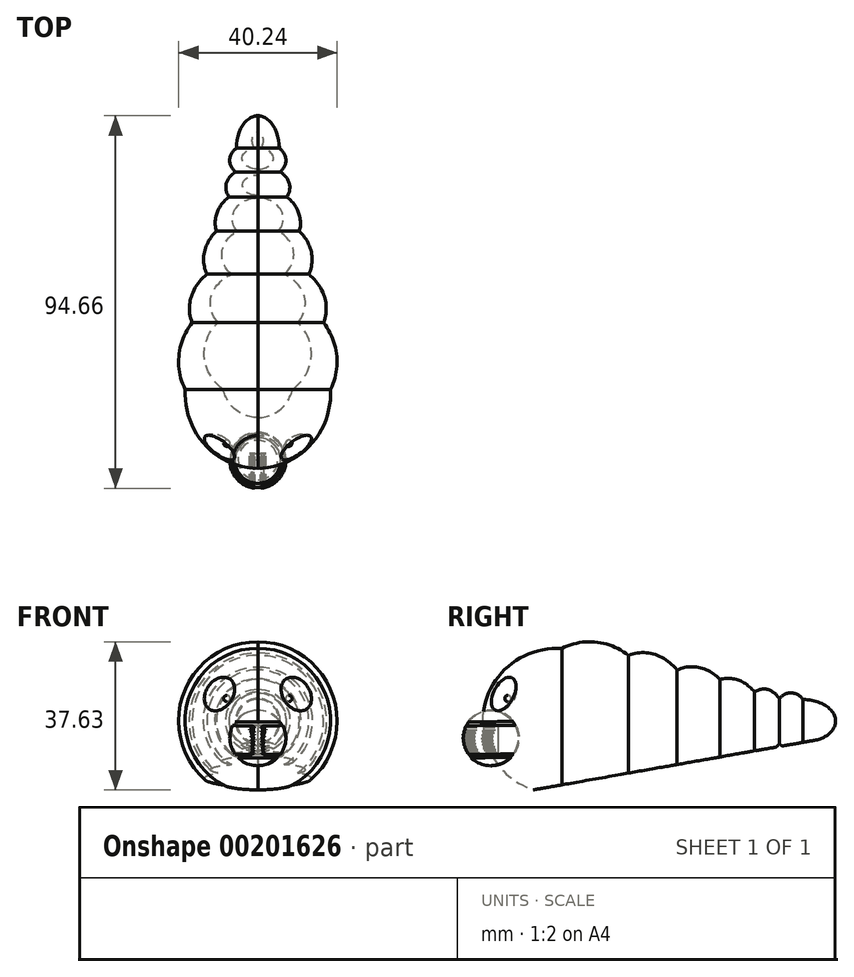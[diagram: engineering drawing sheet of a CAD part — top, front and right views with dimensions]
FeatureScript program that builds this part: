
annotation { "Feature Type Name" : "Feature", "Feature Type Description" : "" }
export const myFeature = defineFeature(function(context is Context, id is Id, definition is map)
    precondition{}
    {
        {
            var Q0;
            Q0=qCreatedBy(makeId("Top.planeOp"),FACE);
            var sketch = newSketch(context, id + "F0", { "sketchPlane" : qUnion([Q0])});
            skEllipticalArc(sketch, "E0", {});
            skEllipticalArc(sketch, "E1", {});
            skPoint(sketch, "E1.centerSnap0", {"position": v(0, -21.26) * mm});
            skEllipticalArc(sketch, "E2", {});
            skEllipticalArc(sketch, "E3", {});
            skEllipticalArc(sketch, "E4", {});
            skEllipticalArc(sketch, "E5", {});
            skEllipticalArc(sketch, "E6", {});
            skEllipticalArc(sketch, "E7", {});
            skLineSegment(sketch, "E8", {"start": v(0, 15.02) * mm, "end": v(0, -47.02) * mm});
            skLineSegment(sketch, "E9", {"start": v(0, -66.04) * mm, "end": v(0, 23.55) * mm});
            const initialGuessF0  = {"E0": [0, -0.038948312401771545, -1, 0, 0.0201253741979599, 0.017687600936562343, 2.7319737527427694, 3.735705464207903], "E1": [0, -0.025389280170202255, -1, 0, 0.017381285256523642, 0.012980058674735876, 2.8559072971359845, 3.8713688343084676], "E2": [0, -0.012964989989995956, -1, 0, 0.013778002209999156, 0.01107321615129807, 2.794142284714198, 3.8417705752233933], "E3": [0, -0.003726113587617874, -1, 0, 0.010834074892715644, 0.00903717395902369, 2.906642104325587, 3.9684165475596376], "E4": [0, 0.005311060371405817, -1, 0, 0.008132504217033262, 0.005535526062008481, 2.6956009997515697, 3.9359959156809072], "E5": [0, -0.04702418949455023, -1, 0, 0.01848768108972128, 0.019015910590964333, 1.5707963267948966, 3.195869498983652], "E6": [0, 0.012173164635896683, -1, 0, 0.007152805326904107, 0.0048193785957226605, 2.4925865913491534, 3.8422771913521236], "E7": [0, 0.015022817999124527, 0, -1, 0.008524764502291721, 0.005470109626082388, 1.6010185470610119, 3.141592653589793]};
            skSetInitialGuess(sketch, initialGuessF0);
            skSolve(sketch);
        }
        {
            var Q0;
            Q0=makeQuery(id+"F0.imprint","IMPRINT",FACE,{"disambiguationData":[TD([[makeQuery(id+"F0.imprint","IMPRINT",EDGE,{"derivedFrom":sQuery(id+"F0.wireOp",EDGE,"E0")}),1.0]])]});
            var Q1;
            Q1=sQuery(id+"F0.wireOp",EDGE,"E9");
            revolve(context, id + "F1", {"entities" : qUnion([Q0]), "axis" : qUnion([Q1]), "revolveType" : RevolveType.SYMMETRIC, "oppositeDirection" : true, "angle" : 180 * degree});
        }
        {
            var Q0;
            Q0=qCreatedBy(makeId("Top.planeOp"),FACE);
            cPlane(context, id + "F2", {"entities" : qUnion([Q0]), "cplaneType" : CPlaneType.OFFSET, "offset" : 8 * mm, "width" : 150 * mm, "height" : 150 * mm});
        }
        {
            var Q0;
            Q0=qCreatedBy(id+"F2.planeOp",FACE);
            var sketch = newSketch(context, id + "F3", { "sketchPlane" : qUnion([Q0])});
            skArc(sketch, "E10", {"start": v(11.4, -57.45) * mm, "mid": v(5.9, -62.94) * mm, "end": v(11.4, -68.44) * mm});
            skLineSegment(sketch, "E11", {"start": v(11.4, -68.44) * mm, "end": v(11.4, -62.94) * mm});
            skLineSegment(sketch, "E12", {"start": v(11.4, -62.94) * mm, "end": v(11.4, -57.45) * mm});
            skSolve(sketch);
        }
        {
            var Q0;
            Q0=makeQuery(id+"F3.imprint","IMPRINT",FACE,{"disambiguationData":[TD([[makeQuery(id+"F3.imprint","IMPRINT",EDGE,{"derivedFrom":sQuery(id+"F3.wireOp",EDGE,"E10")}),1.0]])]});
            var Q1;
            Q1=sQuery(id+"F3.wireOp",EDGE,"E11");
            revolve(context, id + "F4", {"entities" : qUnion([Q0]), "axis" : qUnion([Q1]), "revolveType" : RevolveType.FULL});
        }
        {
            var Q0;
            Q0=makeQuery(id+"F1.opRevolve","SWEPT_BODY",BODY,{"disambiguationData":[OSD([sQuery(id+"F0.wireOp",EDGE,"E0"),sQuery(id+"F0.wireOp",EDGE,"E1"),sQuery(id+"F0.wireOp",EDGE,"E2"),sQuery(id+"F0.wireOp",EDGE,"E3"),sQuery(id+"F0.wireOp",EDGE,"E4"),sQuery(id+"F0.wireOp",EDGE,"E5"),sQuery(id+"F0.wireOp",EDGE,"E6"),sQuery(id+"F0.wireOp",EDGE,"E7"),sQuery(id+"F0.wireOp",EDGE,"E9")])]});
            var Q1;
            Q1=makeQuery(id+"F1.opRevolve","CAP_FACE",FACE,{"disambiguationData":[OSD([sQuery(id+"F0.wireOp",EDGE,"E0"),sQuery(id+"F0.wireOp",EDGE,"E1"),sQuery(id+"F0.wireOp",EDGE,"E2"),sQuery(id+"F0.wireOp",EDGE,"E3"),sQuery(id+"F0.wireOp",EDGE,"E4"),sQuery(id+"F0.wireOp",EDGE,"E5"),sQuery(id+"F0.wireOp",EDGE,"E6"),sQuery(id+"F0.wireOp",EDGE,"E7"),sQuery(id+"F0.wireOp",EDGE,"E9")])],"isStart":false});
            mirror(context, id + "F5", {"entities" : qUnion([Q0]), "mirrorPlane" : qUnion([Q1])});
        }
        {
            var Q0;
            Q0=makeQuery(id+"F5.opPattern","COPY",BODY,{"derivedFrom":makeQuery(id+"F1.opRevolve","SWEPT_BODY",BODY,{"disambiguationData":[OSD([sQuery(id+"F0.wireOp",EDGE,"E0"),sQuery(id+"F0.wireOp",EDGE,"E1"),sQuery(id+"F0.wireOp",EDGE,"E2"),sQuery(id+"F0.wireOp",EDGE,"E3"),sQuery(id+"F0.wireOp",EDGE,"E4"),sQuery(id+"F0.wireOp",EDGE,"E5"),sQuery(id+"F0.wireOp",EDGE,"E6"),sQuery(id+"F0.wireOp",EDGE,"E7"),sQuery(id+"F0.wireOp",EDGE,"E9")])]}),"instanceName":"1"});
            deleteBodies(context, id + "F6", {"entities" : qUnion([Q0])});
        }
        {
            var Q0;
            Q0=makeQuery(id+"F4.opRevolve","SWEPT_BODY",BODY,{"disambiguationData":[OSD([sQuery(id+"F3.wireOp",EDGE,"E10"),sQuery(id+"F3.wireOp",EDGE,"E11"),sQuery(id+"F3.wireOp",EDGE,"E12")])]});
            var Q1;
            Q1=makeQuery(id+"F1.opRevolve","SWEPT_BODY",BODY,{"disambiguationData":[OSD([sQuery(id+"F0.wireOp",EDGE,"E0"),sQuery(id+"F0.wireOp",EDGE,"E1"),sQuery(id+"F0.wireOp",EDGE,"E2"),sQuery(id+"F0.wireOp",EDGE,"E3"),sQuery(id+"F0.wireOp",EDGE,"E4"),sQuery(id+"F0.wireOp",EDGE,"E5"),sQuery(id+"F0.wireOp",EDGE,"E6"),sQuery(id+"F0.wireOp",EDGE,"E7"),sQuery(id+"F0.wireOp",EDGE,"E9")])]});
            booleanBodies(context, id + "F7", {"operationType" : BooleanOperationType.SUBTRACTION, "tools" : qUnion([Q0]), "targets" : qUnion([Q1])});
        }
        {
            var Q0;
            Q0=qCreatedBy(makeId("Top.planeOp"),FACE);
            cPlane(context, id + "F8", {"entities" : qUnion([Q0]), "cplaneType" : CPlaneType.OFFSET, "offset" : 15 * mm, "oppositeDirection" : true, "width" : 152.4 * mm, "height" : 152.4 * mm});
        }
        {
            var Q0;
            Q0=qCreatedBy(makeId("Top.planeOp"),FACE);
            var sketch = newSketch(context, id + "F9", { "sketchPlane" : qUnion([Q0])});
            skLineSegment(sketch, "E13", {"start": v(-16.8, 0) * mm, "end": v(-79.85, 0) * mm});
            skSolve(sketch);
        }
        {
            var Q0;
            Q0=sQuery(id+"F9.wireOp",EDGE,"E13");
            var Q1;
            Q1=qCreatedBy(makeId("Top.planeOp"),FACE);
            cPlane(context, id + "F10", {"entities" : qUnion([Q0, Q1]), "cplaneType" : CPlaneType.LINE_ANGLE, "offset" : 25.4 * mm, "angle" : 170 * degree, "width" : 152.4 * mm, "height" : 152.4 * mm});
        }
        {
            var Q0;
            Q0=qCreatedBy(id+"F10.planeOp",FACE);
            cPlane(context, id + "F11", {"entities" : qUnion([Q0]), "cplaneType" : CPlaneType.OFFSET, "offset" : 8 * mm, "oppositeDirection" : true, "width" : 152.4 * mm, "height" : 152.4 * mm});
        }
        {
            var Q0;
            Q0=qCreatedBy(id+"F11.planeOp",FACE);
            var sketch = newSketch(context, id + "F12", { "sketchPlane" : qUnion([Q0])});
            skLineSegment(sketch, "E14.bottom", {"start": v(-227.07, -120.14) * mm, "end": v(140.37, -120.14) * mm});
            skLineSegment(sketch, "E14.top", {"start": v(-227.07, 67.63) * mm, "end": v(140.37, 67.63) * mm});
            skLineSegment(sketch, "E14.left", {"start": v(-227.07, -120.14) * mm, "end": v(-227.07, 67.63) * mm});
            skLineSegment(sketch, "E14.right", {"start": v(140.37, -120.14) * mm, "end": v(140.37, 67.63) * mm});
            skSolve(sketch);
        }
        {
            var Q0;
            Q0=makeQuery(id+"F12.imprint","IMPRINT",FACE,{"disambiguationData":[TD([[makeQuery(id+"F12.imprint","IMPRINT",EDGE,{"derivedFrom":sQuery(id+"F12.wireOp",EDGE,"E14.bottom")}),1.0]])]});
            extrude(context, id + "F13", {"entities" : qUnion([Q0]), "operationType" : NewBodyOperationType.INTERSECT, "depth" : 127 * mm});
        }
        {
            var Q0;
            Q0=qCreatedBy(makeId("Front.planeOp"),FACE);
            cPlane(context, id + "F14", {"entities" : qUnion([Q0]), "cplaneType" : CPlaneType.OFFSET, "offset" : 59.69 * mm, "width" : 152.4 * mm, "height" : 152.4 * mm});
        }
        {
            var Q0;
            Q0=qCreatedBy(id+"F14.planeOp",FACE);
            var sketch = newSketch(context, id + "F15", { "sketchPlane" : qUnion([Q0])});
            skArc(sketch, "E15", {"start": v(7.86, 6.51) * mm, "mid": v(7.06, 5.7) * mm, "end": v(7.86, 4.9) * mm});
            skLineSegment(sketch, "E16", {"start": v(7.86, 5.7) * mm, "end": v(7.86, 6.51) * mm});
            skLineSegment(sketch, "E17", {"start": v(7.86, 6.51) * mm, "end": v(7.86, 4.9) * mm});
            skSolve(sketch);
        }
        {
            var Q0;
            {var subQ0=sQuery(id+"F15.wireOp",EDGE,"E15");Q0=makeQuery(id+"F15.imprint","IMPRINT",FACE,{"disambiguationData":[TD([[makeQuery(id+"F15.imprint","IMPRINT",EDGE,{"derivedFrom":subQ0}),1.0]])]});}
            var Q1;
            Q1=sQuery(id+"F15.wireOp",EDGE,"E17");
            revolve(context, id + "F16", {"entities" : qUnion([Q0]), "axis" : qUnion([Q1]), "revolveType" : RevolveType.FULL});
        }
        {
            var Q0;
            Q0=qCreatedBy(id+"F14.planeOp",FACE);
            cPlane(context, id + "F17", {"entities" : qUnion([Q0]), "cplaneType" : CPlaneType.OFFSET, "offset" : 2.54 * mm, "width" : 152.4 * mm, "height" : 152.4 * mm});
        }
        {
            var Q0;
            Q0=makeQuery(id+"F1.opRevolve","CAP_FACE",FACE,{"disambiguationData":[OSD([sQuery(id+"F0.wireOp",EDGE,"E0"),sQuery(id+"F0.wireOp",EDGE,"E1"),sQuery(id+"F0.wireOp",EDGE,"E2"),sQuery(id+"F0.wireOp",EDGE,"E3"),sQuery(id+"F0.wireOp",EDGE,"E4"),sQuery(id+"F0.wireOp",EDGE,"E5"),sQuery(id+"F0.wireOp",EDGE,"E6"),sQuery(id+"F0.wireOp",EDGE,"E7"),sQuery(id+"F0.wireOp",EDGE,"E9")])],"isStart":false});
            cPlane(context, id + "F18", {"entities" : qUnion([Q0]), "cplaneType" : CPlaneType.OFFSET, "offset" : 0 * mm, "width" : 152.4 * mm, "height" : 152.4 * mm});
        }
        {
            var Q0;
            Q0=qCreatedBy(id+"F18.planeOp",FACE);
            var sketch = newSketch(context, id + "F19", { "sketchPlane" : qUnion([Q0])});
            skArc(sketch, "E18", {"start": v(63.94, -11.36) * mm, "mid": v(66.69, -10.88) * mm, "end": v(69.03, -9.37) * mm});
            skLineSegment(sketch, "E19", {"start": v(69.86, -0.27) * mm, "end": v(64.08, -0.27) * mm});
            skLineSegment(sketch, "E20", {"start": v(63.97, -9.37) * mm, "end": v(69.03, -9.37) * mm});
            skLineSegment(sketch, "E21", {"start": v(63.98, -8.54) * mm, "end": v(69.76, -8.54) * mm});
            skLineSegment(sketch, "E22", {"start": v(64.07, -1.24) * mm, "end": v(70.44, -1.24) * mm});
            skArc(sketch, "E23.trimOffspring", {"start": v(69.86, -0.27) * mm, "mid": v(67.35, 1.91) * mm, "end": v(64.12, 2.7) * mm});
            skArc(sketch, "E24.trimOffspring", {"start": v(69.76, -8.54) * mm, "mid": v(71.12, -4.98) * mm, "end": v(70.44, -1.24) * mm});
            skLineSegment(sketch, "E25", {"start": v(64.12, 2.7) * mm, "end": v(63.94, -11.36) * mm});
            skSolve(sketch);
        }
        {
            var Q0;
            {var subQ0=sQuery(id+"F19.wireOp",EDGE,"E21");Q0=makeQuery(id+"F19.imprint","IMPRINT",FACE,{"disambiguationData":[TD([[makeQuery(id+"F19.imprint","IMPRINT",EDGE,{"derivedFrom":subQ0}),1.0]])]});}
            var Q1;
            {var subQ0=sQuery(id+"F19.wireOp",EDGE,"E18");Q1=makeQuery(id+"F19.imprint","IMPRINT",FACE,{"disambiguationData":[TD([[makeQuery(id+"F19.imprint","IMPRINT",EDGE,{"derivedFrom":subQ0}),1.0]])]});}
            var Q2;
            {var subQ0=sQuery(id+"F19.wireOp",EDGE,"E19");Q2=makeQuery(id+"F19.imprint","IMPRINT",FACE,{"disambiguationData":[TD([[makeQuery(id+"F19.imprint","IMPRINT",EDGE,{"derivedFrom":subQ0}),-1.0]])]});}
            var Q3;
            Q3=sQuery(id+"F19.wireOp",EDGE,"E25");
            revolve(context, id + "F20", {"entities" : qUnion([Q0, Q1, Q2]), "axis" : qUnion([Q3]), "revolveType" : RevolveType.FULL});
        }
        {
            var Q0;
            Q0=makeQuery(id+"F1.opRevolve","SWEPT_BODY",BODY,{"disambiguationData":[OSD([sQuery(id+"F0.wireOp",EDGE,"E0"),sQuery(id+"F0.wireOp",EDGE,"E1"),sQuery(id+"F0.wireOp",EDGE,"E2"),sQuery(id+"F0.wireOp",EDGE,"E3"),sQuery(id+"F0.wireOp",EDGE,"E4"),sQuery(id+"F0.wireOp",EDGE,"E5"),sQuery(id+"F0.wireOp",EDGE,"E6"),sQuery(id+"F0.wireOp",EDGE,"E7"),sQuery(id+"F0.wireOp",EDGE,"E9")])]});
            var Q1;
            Q1=makeQuery(id+"F16.opRevolve","SWEPT_BODY",BODY,{"disambiguationData":[OSD([sQuery(id+"F15.wireOp",EDGE,"E15"),sQuery(id+"F15.wireOp",EDGE,"E17")])]});
            var Q2;
            Q2=makeQuery(id+"F1.opRevolve","CAP_FACE",FACE,{"disambiguationData":[OSD([sQuery(id+"F0.wireOp",EDGE,"E0"),sQuery(id+"F0.wireOp",EDGE,"E1"),sQuery(id+"F0.wireOp",EDGE,"E2"),sQuery(id+"F0.wireOp",EDGE,"E3"),sQuery(id+"F0.wireOp",EDGE,"E4"),sQuery(id+"F0.wireOp",EDGE,"E5"),sQuery(id+"F0.wireOp",EDGE,"E6"),sQuery(id+"F0.wireOp",EDGE,"E7"),sQuery(id+"F0.wireOp",EDGE,"E9")])],"isStart":false});
            mirror(context, id + "F21", {"entities" : qUnion([Q0, Q1]), "mirrorPlane" : qUnion([Q2])});
        }
        {
            var Q0;
            Q0=qCreatedBy(id+"F17.planeOp",FACE);
            var sketch = newSketch(context, id + "F22", { "sketchPlane" : qUnion([Q0])});
            skLineSegment(sketch, "E26", {"start": v(2.05, -0.9) * mm, "end": v(0.74, -1.67) * mm});
            skLineSegment(sketch, "E27", {"start": v(0.74, -1.67) * mm, "end": v(2.1, -2.22) * mm});
            skLineSegment(sketch, "E28", {"start": v(2.1, -2.22) * mm, "end": v(0.76, -2.57) * mm});
            skLineSegment(sketch, "E29", {"start": v(0.76, -2.57) * mm, "end": v(1.93, -2.98) * mm});
            skLineSegment(sketch, "E30", {"start": v(1.93, -2.98) * mm, "end": v(0.84, -3.5) * mm});
            skLineSegment(sketch, "E31", {"start": v(0.84, -3.5) * mm, "end": v(1.82, -3.94) * mm});
            skLineSegment(sketch, "E32", {"start": v(1.82, -3.94) * mm, "end": v(0.86, -4.38) * mm});
            skLineSegment(sketch, "E33", {"start": v(0.86, -4.38) * mm, "end": v(1.7, -4.88) * mm});
            skLineSegment(sketch, "E34", {"start": v(1.7, -4.88) * mm, "end": v(0.9, -5.22) * mm});
            skLineSegment(sketch, "E35", {"start": v(0.9, -5.22) * mm, "end": v(1.71, -5.68) * mm});
            skLineSegment(sketch, "E36", {"start": v(1.71, -5.68) * mm, "end": v(0.9, -5.96) * mm});
            skLineSegment(sketch, "E37", {"start": v(0.9, -5.96) * mm, "end": v(1.65, -6.47) * mm});
            skLineSegment(sketch, "E38", {"start": v(1.65, -6.47) * mm, "end": v(1, -6.92) * mm});
            skLineSegment(sketch, "E39", {"start": v(1, -6.92) * mm, "end": v(1.67, -7.22) * mm});
            skLineSegment(sketch, "E40", {"start": v(1.67, -7.22) * mm, "end": v(1.04, -7.47) * mm});
            skLineSegment(sketch, "E41", {"start": v(1.04, -7.47) * mm, "end": v(1.6, -7.94) * mm});
            skLineSegment(sketch, "E42", {"start": v(1.6, -7.94) * mm, "end": v(0.93, -8.19) * mm});
            skLineSegment(sketch, "E43", {"start": v(0.93, -8.19) * mm, "end": v(1.62, -8.54) * mm});
            skLineSegment(sketch, "E44", {"start": v(0, 0) * mm, "end": v(0, -11.1) * mm});
            skLineSegment(sketch, "E45", {"start": v(2.05, -0.9) * mm, "end": v(0, 0) * mm});
            skLineSegment(sketch, "E46", {"start": v(1.62, -8.54) * mm, "end": v(0, -11.1) * mm});
            skPoint(sketch, "E47.end.orphan", {"position": v(6.1, 9.28) * mm});
            skPoint(sketch, "E48.start.orphan", {"position": v(10.8, 2.59) * mm});
            skPoint(sketch, "E49.orphan", {"position": v(0, 11.1) * mm});
            skSolve(sketch);
        }
        {
            var Q0;
            Q0 = qSketchRegion(id + "F22", true);
            extrude(context, id + "F23", {"entities" : qUnion([Q0]), "depth" : 25 * mm});
        }
        {
            var Q0;
            Q0=makeQuery(id+"F23.opExtrude","SWEPT_BODY",BODY,{"disambiguationData":[OSD([sQuery(id+"F22.wireOp",EDGE,"E26"),sQuery(id+"F22.wireOp",EDGE,"E27"),sQuery(id+"F22.wireOp",EDGE,"E28"),sQuery(id+"F22.wireOp",EDGE,"E29"),sQuery(id+"F22.wireOp",EDGE,"E30"),sQuery(id+"F22.wireOp",EDGE,"E31"),sQuery(id+"F22.wireOp",EDGE,"E32"),sQuery(id+"F22.wireOp",EDGE,"E33"),sQuery(id+"F22.wireOp",EDGE,"E34"),sQuery(id+"F22.wireOp",EDGE,"E35"),sQuery(id+"F22.wireOp",EDGE,"E36"),sQuery(id+"F22.wireOp",EDGE,"E37"),sQuery(id+"F22.wireOp",EDGE,"E38"),sQuery(id+"F22.wireOp",EDGE,"E39"),sQuery(id+"F22.wireOp",EDGE,"E40"),sQuery(id+"F22.wireOp",EDGE,"E41"),sQuery(id+"F22.wireOp",EDGE,"E42"),sQuery(id+"F22.wireOp",EDGE,"E43"),sQuery(id+"F22.wireOp",EDGE,"E44"),sQuery(id+"F22.wireOp",EDGE,"E45"),sQuery(id+"F22.wireOp",EDGE,"E46")])]});
            var Q1;
            Q1=makeQuery(id+"F23.opExtrude","SWEPT_FACE",FACE,{"disambiguationData":[OSD([sQuery(id+"F22.wireOp",EDGE,"E44")])]});
            mirror(context, id + "F24", {"entities" : qUnion([Q0]), "mirrorPlane" : qUnion([Q1])});
        }
        {
            var Q0;
            Q0=makeQuery(id+"F24.opPattern","COPY",BODY,{"derivedFrom":makeQuery(id+"F23.opExtrude","SWEPT_BODY",BODY,{"disambiguationData":[OSD([sQuery(id+"F22.wireOp",EDGE,"E26"),sQuery(id+"F22.wireOp",EDGE,"E27"),sQuery(id+"F22.wireOp",EDGE,"E28"),sQuery(id+"F22.wireOp",EDGE,"E29"),sQuery(id+"F22.wireOp",EDGE,"E30"),sQuery(id+"F22.wireOp",EDGE,"E31"),sQuery(id+"F22.wireOp",EDGE,"E32"),sQuery(id+"F22.wireOp",EDGE,"E33"),sQuery(id+"F22.wireOp",EDGE,"E34"),sQuery(id+"F22.wireOp",EDGE,"E35"),sQuery(id+"F22.wireOp",EDGE,"E36"),sQuery(id+"F22.wireOp",EDGE,"E37"),sQuery(id+"F22.wireOp",EDGE,"E38"),sQuery(id+"F22.wireOp",EDGE,"E39"),sQuery(id+"F22.wireOp",EDGE,"E40"),sQuery(id+"F22.wireOp",EDGE,"E41"),sQuery(id+"F22.wireOp",EDGE,"E42"),sQuery(id+"F22.wireOp",EDGE,"E43"),sQuery(id+"F22.wireOp",EDGE,"E44"),sQuery(id+"F22.wireOp",EDGE,"E45"),sQuery(id+"F22.wireOp",EDGE,"E46")])]}),"instanceName":"1"});
            var Q1;
            Q1=makeQuery(id+"F23.opExtrude","SWEPT_BODY",BODY,{"disambiguationData":[OSD([sQuery(id+"F22.wireOp",EDGE,"E26"),sQuery(id+"F22.wireOp",EDGE,"E27"),sQuery(id+"F22.wireOp",EDGE,"E28"),sQuery(id+"F22.wireOp",EDGE,"E29"),sQuery(id+"F22.wireOp",EDGE,"E30"),sQuery(id+"F22.wireOp",EDGE,"E31"),sQuery(id+"F22.wireOp",EDGE,"E32"),sQuery(id+"F22.wireOp",EDGE,"E33"),sQuery(id+"F22.wireOp",EDGE,"E34"),sQuery(id+"F22.wireOp",EDGE,"E35"),sQuery(id+"F22.wireOp",EDGE,"E36"),sQuery(id+"F22.wireOp",EDGE,"E37"),sQuery(id+"F22.wireOp",EDGE,"E38"),sQuery(id+"F22.wireOp",EDGE,"E39"),sQuery(id+"F22.wireOp",EDGE,"E40"),sQuery(id+"F22.wireOp",EDGE,"E41"),sQuery(id+"F22.wireOp",EDGE,"E42"),sQuery(id+"F22.wireOp",EDGE,"E43"),sQuery(id+"F22.wireOp",EDGE,"E44"),sQuery(id+"F22.wireOp",EDGE,"E45"),sQuery(id+"F22.wireOp",EDGE,"E46")])]});
            var Q2;
            Q2=makeQuery(id+"F20.opRevolve","SWEPT_BODY",BODY,{"disambiguationData":[OSD([sQuery(id+"F19.wireOp",EDGE,"E21"),sQuery(id+"F19.wireOp",EDGE,"E22"),sQuery(id+"F19.wireOp",EDGE,"E24.trimOffspring"),sQuery(id+"F19.wireOp",EDGE,"E25")])]});
            booleanBodies(context, id + "F25", {"operationType" : BooleanOperationType.SUBTRACTION, "tools" : qUnion([Q0, Q1]), "targets" : qUnion([Q2])});
        }
    });
